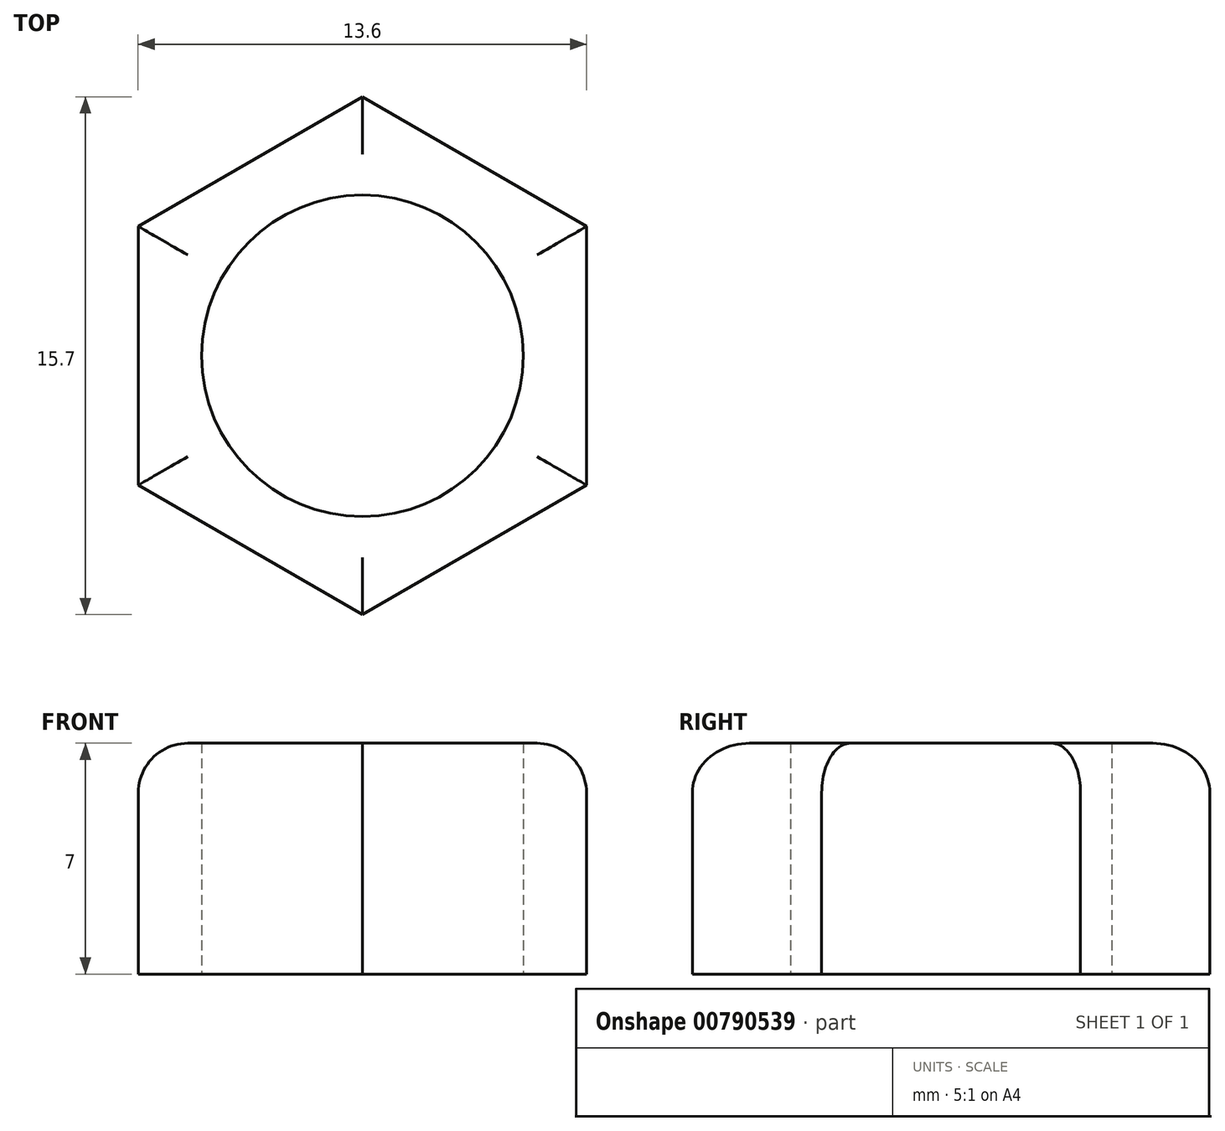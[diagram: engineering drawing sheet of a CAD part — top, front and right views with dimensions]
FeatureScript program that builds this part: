
annotation { "Feature Type Name" : "Feature", "Feature Type Description" : "" }
export const myFeature = defineFeature(function(context is Context, id is Id, definition is map)
    precondition{}
    {
        {
            var Q0;
            Q0=qCreatedBy(makeId("Top.planeOp"),FACE);
            var sketch = newSketch(context, id + "F0", { "sketchPlane" : qUnion([Q0])});
            skCircle(sketch, "E0.cCircle", {"center": v(0, 0) * mm, "radius": 6.8 * mm, "construction": true});
            skLineSegment(sketch, "E0.0", {"start": v(0, 7.85) * mm, "end": v(6.8, 3.92) * mm});
            skLineSegment(sketch, "E0.1", {"start": v(6.8, 3.92) * mm, "end": v(6.8, -3.92) * mm});
            skLineSegment(sketch, "E0.2", {"start": v(6.8, -3.92) * mm, "end": v(0, -7.85) * mm});
            skLineSegment(sketch, "E0.3", {"start": v(0, -7.85) * mm, "end": v(-6.8, -3.92) * mm});
            skLineSegment(sketch, "E0.4", {"start": v(-6.8, -3.92) * mm, "end": v(-6.8, 3.92) * mm});
            skLineSegment(sketch, "E0.5", {"start": v(-6.8, 3.92) * mm, "end": v(0, 7.85) * mm});
            skPoint(sketch, "E0.0.midPoint", {"position": v(3.4, 5.89) * mm});
            skCircle(sketch, "E1", {"center": v(0, 0) * mm, "radius": 4.87 * mm});
            skSolve(sketch);
        }
        {
            var Q0;
            Q0=makeQuery(id+"F0.imprint","IMPRINT",FACE,{"disambiguationData":[TD([[makeQuery(id+"F0.imprint","IMPRINT",EDGE,{"derivedFrom":sQuery(id+"F0.wireOp",EDGE,"E0.0")}),-1.0]])]});
            extrude(context, id + "F1", {"entities" : qUnion([Q0]), "depth" : 7 * mm, "offsetDistance" : 25 * mm});
        }
        {
            var Q0;
            Q0=makeQuery(id+"F1.opExtrude","CAP_EDGE",EDGE,{"disambiguationData":[OSD([sQuery(id+"F0.wireOp",EDGE,"E0.1")])],"isStart":false});
            var Q1;
            Q1=makeQuery(id+"F1.opExtrude","CAP_EDGE",EDGE,{"disambiguationData":[OSD([sQuery(id+"F0.wireOp",EDGE,"E0.2")])],"isStart":false});
            var Q2;
            Q2=makeQuery(id+"F1.opExtrude","CAP_EDGE",EDGE,{"disambiguationData":[OSD([sQuery(id+"F0.wireOp",EDGE,"E0.3")])],"isStart":false});
            var Q3;
            Q3=makeQuery(id+"F1.opExtrude","CAP_EDGE",EDGE,{"disambiguationData":[OSD([sQuery(id+"F0.wireOp",EDGE,"E0.0")])],"isStart":false});
            var Q4;
            Q4=makeQuery(id+"F1.opExtrude","CAP_EDGE",EDGE,{"disambiguationData":[OSD([sQuery(id+"F0.wireOp",EDGE,"E0.4")])],"isStart":false});
            var Q5;
            Q5=makeQuery(id+"F1.opExtrude","CAP_EDGE",EDGE,{"disambiguationData":[OSD([sQuery(id+"F0.wireOp",EDGE,"E0.5")])],"isStart":false});
            fillet(context, id + "F2", {"entities" : qUnion([Q0, Q1, Q2, Q3, Q4, Q5]), "radius" : 1.5 * mm, "tangentPropagation" : true, "allowEdgeOverflow" : false});
        }
    });
